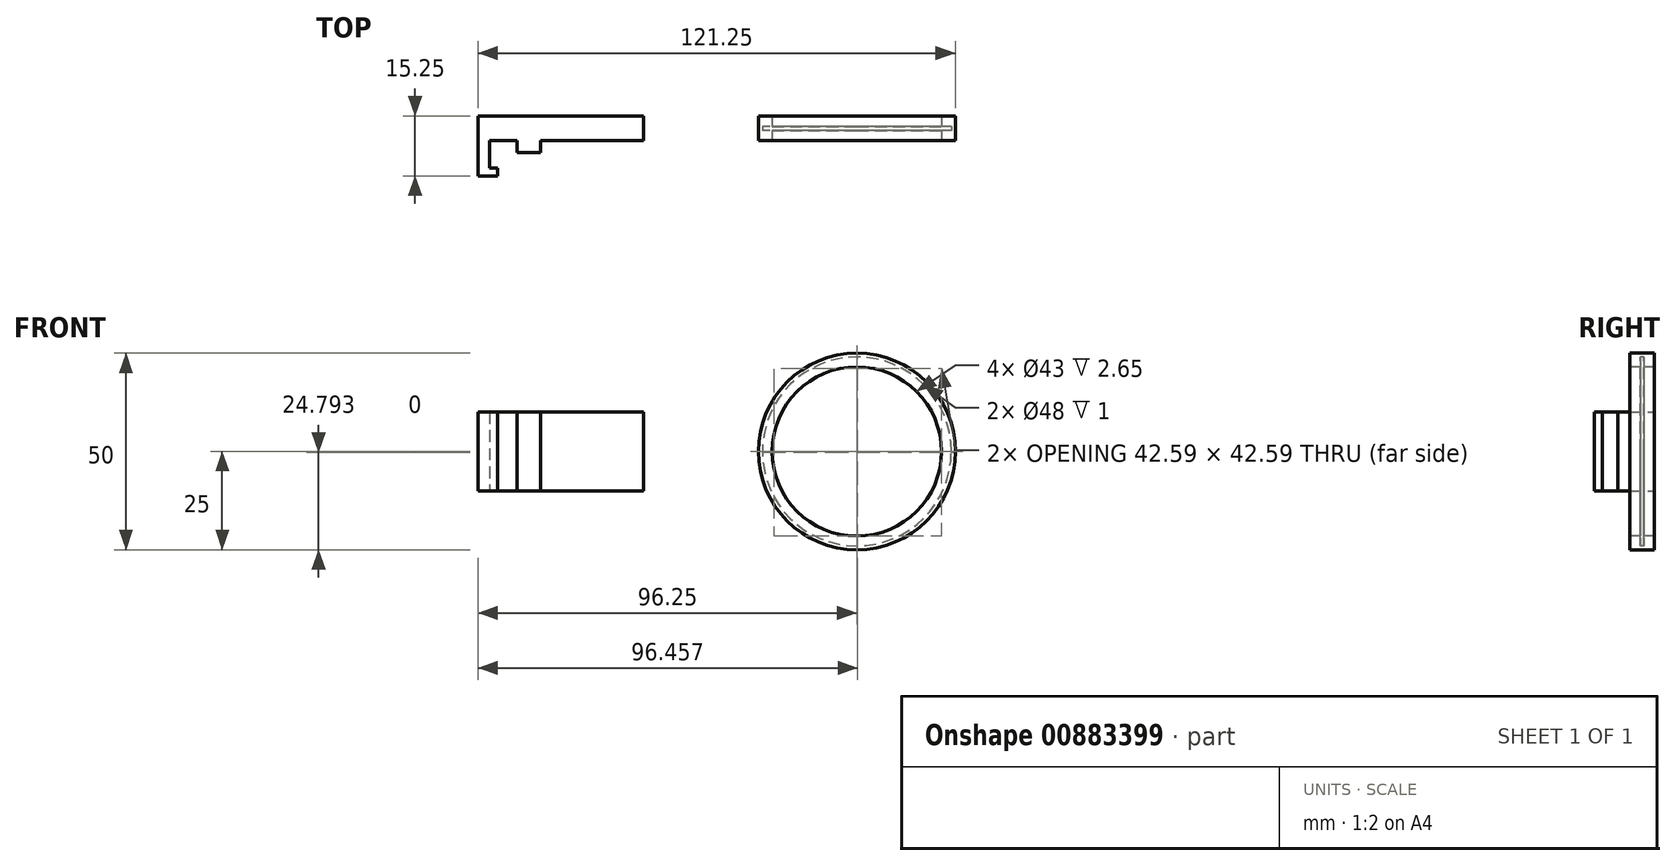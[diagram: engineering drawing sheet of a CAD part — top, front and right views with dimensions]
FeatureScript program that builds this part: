
annotation { "Feature Type Name" : "Feature", "Feature Type Description" : "" }
export const myFeature = defineFeature(function(context is Context, id is Id, definition is map)
    precondition{}
    {
        {
            var Q0;
            Q0=qCreatedBy(makeId("Front.planeOp"),FACE);
            var sketch = newSketch(context, id + "F0", { "sketchPlane" : qUnion([Q0])});
            skCircle(sketch, "E0", {"center": v(0, 0) * mm, "radius": 25 * mm});
            skCircle(sketch, "E1", {"center": v(0, 0) * mm, "radius": 21.5 * mm});
            skLineSegment(sketch, "E2", {"start": v(-23.02, 9.74) * mm, "end": v(-39.05, 9.74) * mm});
            skLineSegment(sketch, "E3", {"start": v(-39.05, 9.74) * mm, "end": v(-39.05, 0) * mm});
            skLineSegment(sketch, "E4.MirrorCS", {"start": v(-23.02, -9.74) * mm, "end": v(-39.05, -9.74) * mm});
            skLineSegment(sketch, "E5.MirrorCS", {"start": v(-39.05, -9.74) * mm, "end": v(-39.05, 0) * mm});
            skSolve(sketch);
        }
        {
            var Q0;
            Q0=makeQuery(id+"F0.imprint","IMPRINT",FACE,{"disambiguationData":[TD([[makeQuery(id+"F0.imprint","IMPRINT",EDGE,{"derivedFrom":sQuery(id+"F0.wireOp",EDGE,"E1")}),-1.0]])]});
            extrude(context, id + "F1", {"entities" : qUnion([Q0]), "endBound" : BoundingType.SYMMETRIC, "oppositeDirection" : true, "depth" : 6.3 * mm, "offsetDistance" : 25 * mm});
        }
        {
            var Q0;
            Q0=qCreatedBy(makeId("Top.planeOp"),FACE);
            var sketch = newSketch(context, id + "F2", { "sketchPlane" : qUnion([Q0])});
            skLineSegment(sketch, "E6", {"start": v(21.5, -0.5) * mm, "end": v(21.5, 0.5) * mm});
            skLineSegment(sketch, "E7", {"start": v(21.5, -0.5) * mm, "end": v(24, -0.5) * mm});
            skLineSegment(sketch, "E8", {"start": v(24, -0.5) * mm, "end": v(24, 0.5) * mm});
            skLineSegment(sketch, "E9", {"start": v(24, 0.5) * mm, "end": v(21.5, 0.5) * mm});
            skLineSegment(sketch, "E10.0", {"start": v(21.5, 0) * mm, "end": v(-21.5, 0) * mm});
            skSolve(sketch);
        }
        {
            var Q0;
            Q0 = qSketchRegion(id + "F2", true);
            var Q1;
            Q1=sQuery(id+"F0.wireOp",EDGE,"E1");
            sweep(context, id + "F3", {"operationType" : NewBodyOperationType.REMOVE, "profiles" : qUnion([Q0]), "path" : qUnion([Q1])});
        }
        {
            var Q0;
            Q0=qCreatedBy(makeId("Top.planeOp"),FACE);
            var sketch = newSketch(context, id + "F4", { "sketchPlane" : qUnion([Q0])});
            skLineSegment(sketch, "E11", {"start": v(-54.25, 3.16) * mm, "end": v(-96.25, 3.16) * mm});
            skLineSegment(sketch, "E12", {"start": v(-96.25, 3.16) * mm, "end": v(-96.25, -12.09) * mm});
            skLineSegment(sketch, "E13", {"start": v(-96.25, -12.09) * mm, "end": v(-91.25, -12.09) * mm});
            skLineSegment(sketch, "E14", {"start": v(-93.25, -3.14) * mm, "end": v(-86.3, -3.14) * mm});
            skLineSegment(sketch, "E15", {"start": v(-54.25, -3.14) * mm, "end": v(-54.25, 3.16) * mm});
            skLineSegment(sketch, "E16", {"start": v(-86.3, -3.14) * mm, "end": v(-86.3, -6.14) * mm});
            skLineSegment(sketch, "E17", {"start": v(-86.3, -6.14) * mm, "end": v(-80.4, -6.14) * mm});
            skLineSegment(sketch, "E18", {"start": v(-80.4, -6.14) * mm, "end": v(-80.4, -3.14) * mm});
            skLineSegment(sketch, "E19.trimOffspring", {"start": v(-80.4, -3.14) * mm, "end": v(-54.25, -3.14) * mm});
            skLineSegment(sketch, "E20", {"start": v(-91.25, -12.09) * mm, "end": v(-91.25, -10.09) * mm});
            skLineSegment(sketch, "E21", {"start": v(-91.25, -10.09) * mm, "end": v(-93.25, -10.09) * mm});
            skLineSegment(sketch, "E22", {"start": v(-93.25, -10.09) * mm, "end": v(-93.25, -3.14) * mm});
            skSolve(sketch);
        }
        {
            var Q0;
            Q0 = qSketchRegion(id + "F4", true);
            extrude(context, id + "F5", {"entities" : qUnion([Q0]), "endBound" : BoundingType.SYMMETRIC, "depth" : 20 * mm, "offsetDistance" : 25 * mm});
        }
    });
